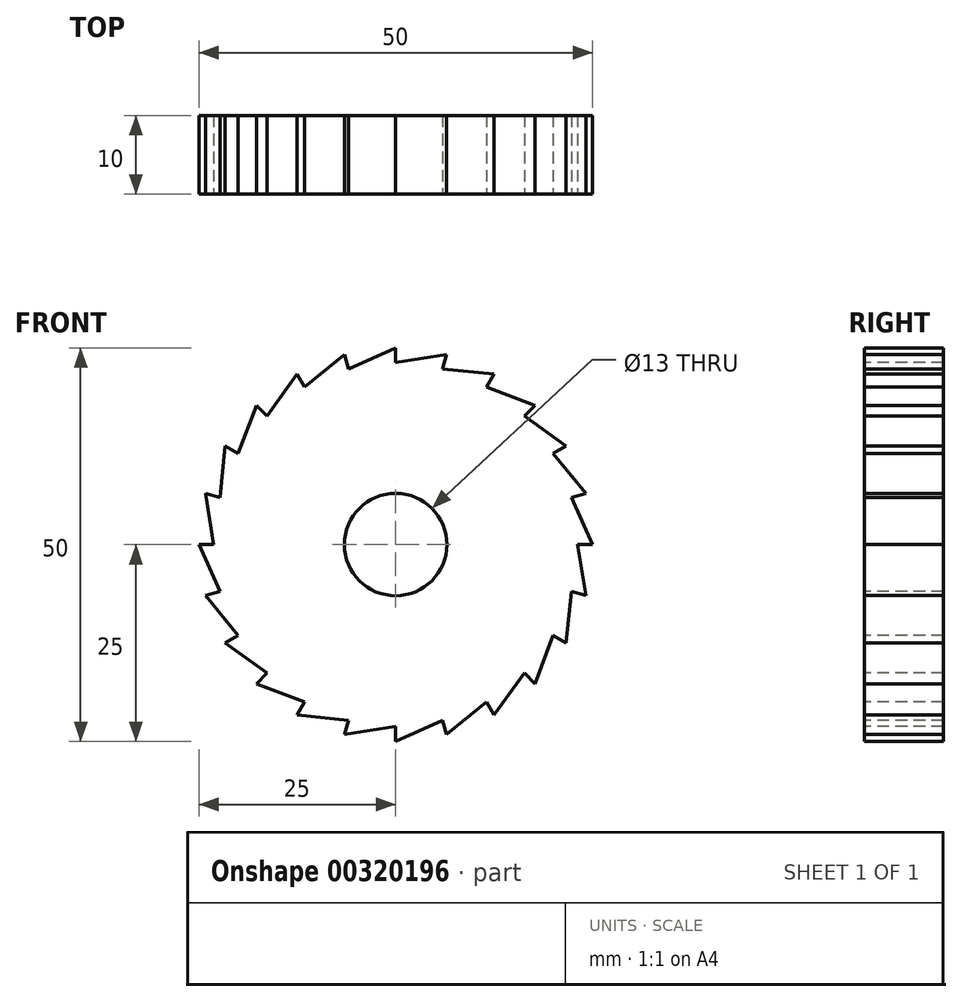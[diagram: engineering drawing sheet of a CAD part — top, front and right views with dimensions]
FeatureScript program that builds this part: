
annotation { "Feature Type Name" : "Feature", "Feature Type Description" : "" }
export const myFeature = defineFeature(function(context is Context, id is Id, definition is map)
    precondition{}
    {
        {
            var Q0;
            Q0=qCreatedBy(makeId("Front.planeOp"),FACE);
            var sketch = newSketch(context, id + "F0", { "sketchPlane" : qUnion([Q0])});
            skLineSegment(sketch, "E0", {"start": v(0, 25) * mm, "end": v(0, 23.1) * mm});
            skLineSegment(sketch, "E1", {"start": v(0, 23.1) * mm, "end": v(6.47, 24.15) * mm});
            skLineSegment(sketch, "E2.1.0", {"start": v(-5.98, 22.31) * mm, "end": v(0, 25) * mm});
            skLineSegment(sketch, "E2.1.1", {"start": v(-6.47, 24.15) * mm, "end": v(-5.98, 22.31) * mm});
            skLineSegment(sketch, "E2.2.0", {"start": v(-11.55, 20) * mm, "end": v(-6.47, 24.15) * mm});
            skLineSegment(sketch, "E2.2.1", {"start": v(-12.5, 21.65) * mm, "end": v(-11.55, 20) * mm});
            skLineSegment(sketch, "E2.3.0", {"start": v(-16.33, 16.33) * mm, "end": v(-12.5, 21.65) * mm});
            skLineSegment(sketch, "E2.3.1", {"start": v(-17.68, 17.68) * mm, "end": v(-16.33, 16.33) * mm});
            skLineSegment(sketch, "E2.4.0", {"start": v(-20, 11.55) * mm, "end": v(-17.68, 17.68) * mm});
            skLineSegment(sketch, "E2.4.1", {"start": v(-21.65, 12.5) * mm, "end": v(-20, 11.55) * mm});
            skLineSegment(sketch, "E2.5.0", {"start": v(-22.31, 5.98) * mm, "end": v(-21.65, 12.5) * mm});
            skLineSegment(sketch, "E2.5.1", {"start": v(-24.15, 6.47) * mm, "end": v(-22.31, 5.98) * mm});
            skLineSegment(sketch, "E2.6.0", {"start": v(-23.1, 0) * mm, "end": v(-24.15, 6.47) * mm});
            skLineSegment(sketch, "E2.6.1", {"start": v(-25, 0) * mm, "end": v(-23.1, 0) * mm});
            skLineSegment(sketch, "E2.7.0", {"start": v(-22.31, -5.98) * mm, "end": v(-25, 0) * mm});
            skLineSegment(sketch, "E2.7.1", {"start": v(-24.15, -6.47) * mm, "end": v(-22.31, -5.98) * mm});
            skLineSegment(sketch, "E2.8.0", {"start": v(-20, -11.55) * mm, "end": v(-24.15, -6.47) * mm});
            skLineSegment(sketch, "E2.8.1", {"start": v(-21.65, -12.5) * mm, "end": v(-20, -11.55) * mm});
            skLineSegment(sketch, "E2.9.0", {"start": v(-16.33, -16.33) * mm, "end": v(-21.65, -12.5) * mm});
            skLineSegment(sketch, "E2.9.1", {"start": v(-17.68, -17.68) * mm, "end": v(-16.33, -16.33) * mm});
            skLineSegment(sketch, "E2.10.0", {"start": v(-11.55, -20) * mm, "end": v(-17.68, -17.68) * mm});
            skLineSegment(sketch, "E2.10.1", {"start": v(-12.5, -21.65) * mm, "end": v(-11.55, -20) * mm});
            skLineSegment(sketch, "E2.11.0", {"start": v(-5.98, -22.31) * mm, "end": v(-12.5, -21.65) * mm});
            skLineSegment(sketch, "E2.11.1", {"start": v(-6.47, -24.15) * mm, "end": v(-5.98, -22.31) * mm});
            skLineSegment(sketch, "E2.12.0", {"start": v(0, -23.1) * mm, "end": v(-6.47, -24.15) * mm});
            skLineSegment(sketch, "E2.12.1", {"start": v(0, -25) * mm, "end": v(0, -23.1) * mm});
            skLineSegment(sketch, "E2.13.0", {"start": v(5.98, -22.31) * mm, "end": v(0, -25) * mm});
            skLineSegment(sketch, "E2.13.1", {"start": v(6.47, -24.15) * mm, "end": v(5.98, -22.31) * mm});
            skLineSegment(sketch, "E2.14.0", {"start": v(11.55, -20) * mm, "end": v(6.47, -24.15) * mm});
            skLineSegment(sketch, "E2.14.1", {"start": v(12.5, -21.65) * mm, "end": v(11.55, -20) * mm});
            skLineSegment(sketch, "E2.15.0", {"start": v(16.33, -16.33) * mm, "end": v(12.5, -21.65) * mm});
            skLineSegment(sketch, "E2.15.1", {"start": v(17.68, -17.68) * mm, "end": v(16.33, -16.33) * mm});
            skLineSegment(sketch, "E2.16.0", {"start": v(20, -11.55) * mm, "end": v(17.68, -17.68) * mm});
            skLineSegment(sketch, "E2.16.1", {"start": v(21.65, -12.5) * mm, "end": v(20, -11.55) * mm});
            skLineSegment(sketch, "E2.17.0", {"start": v(22.31, -5.98) * mm, "end": v(21.65, -12.5) * mm});
            skLineSegment(sketch, "E2.17.1", {"start": v(24.15, -6.47) * mm, "end": v(22.31, -5.98) * mm});
            skLineSegment(sketch, "E2.18.0", {"start": v(23.1, 0) * mm, "end": v(24.15, -6.47) * mm});
            skLineSegment(sketch, "E2.18.1", {"start": v(25, 0) * mm, "end": v(23.1, 0) * mm});
            skLineSegment(sketch, "E2.19.0", {"start": v(22.31, 5.98) * mm, "end": v(25, 0) * mm});
            skLineSegment(sketch, "E2.19.1", {"start": v(24.15, 6.47) * mm, "end": v(22.31, 5.98) * mm});
            skPoint(sketch, "E2.center", {"position": v(0, 0) * mm});
            skLineSegment(sketch, "E3.1.20.0", {"start": v(20, 11.55) * mm, "end": v(24.15, 6.47) * mm});
            skLineSegment(sketch, "E3.3.20.0", {"start": v(21.65, 12.5) * mm, "end": v(20, 11.55) * mm});
            skLineSegment(sketch, "E4.1.21.0", {"start": v(16.33, 16.33) * mm, "end": v(21.65, 12.5) * mm});
            skLineSegment(sketch, "E4.3.21.0", {"start": v(17.68, 17.68) * mm, "end": v(16.33, 16.33) * mm});
            skLineSegment(sketch, "E5.1.22.0", {"start": v(11.55, 20) * mm, "end": v(17.68, 17.68) * mm});
            skLineSegment(sketch, "E5.3.22.0", {"start": v(12.5, 21.65) * mm, "end": v(11.55, 20) * mm});
            skCircle(sketch, "E6", {"center": v(0, 0) * mm, "radius": 6.5 * mm});
            skLineSegment(sketch, "E7.1.23.0", {"start": v(5.98, 22.31) * mm, "end": v(12.5, 21.65) * mm});
            skLineSegment(sketch, "E7.3.23.0", {"start": v(6.47, 24.15) * mm, "end": v(5.98, 22.31) * mm});
            skSolve(sketch);
        }
        {
            var Q0;
            Q0=makeQuery(id+"F0.imprint","IMPRINT",FACE,{"disambiguationData":[TD([[makeQuery(id+"F0.imprint","IMPRINT",EDGE,{"derivedFrom":sQuery(id+"F0.wireOp",EDGE,"E0")}),-1.0]])]});
            extrude(context, id + "F1", {"entities" : qUnion([Q0]), "endBound" : BoundingType.SYMMETRIC, "oppositeDirection" : true, "depth" : 10 * mm});
        }
    });
